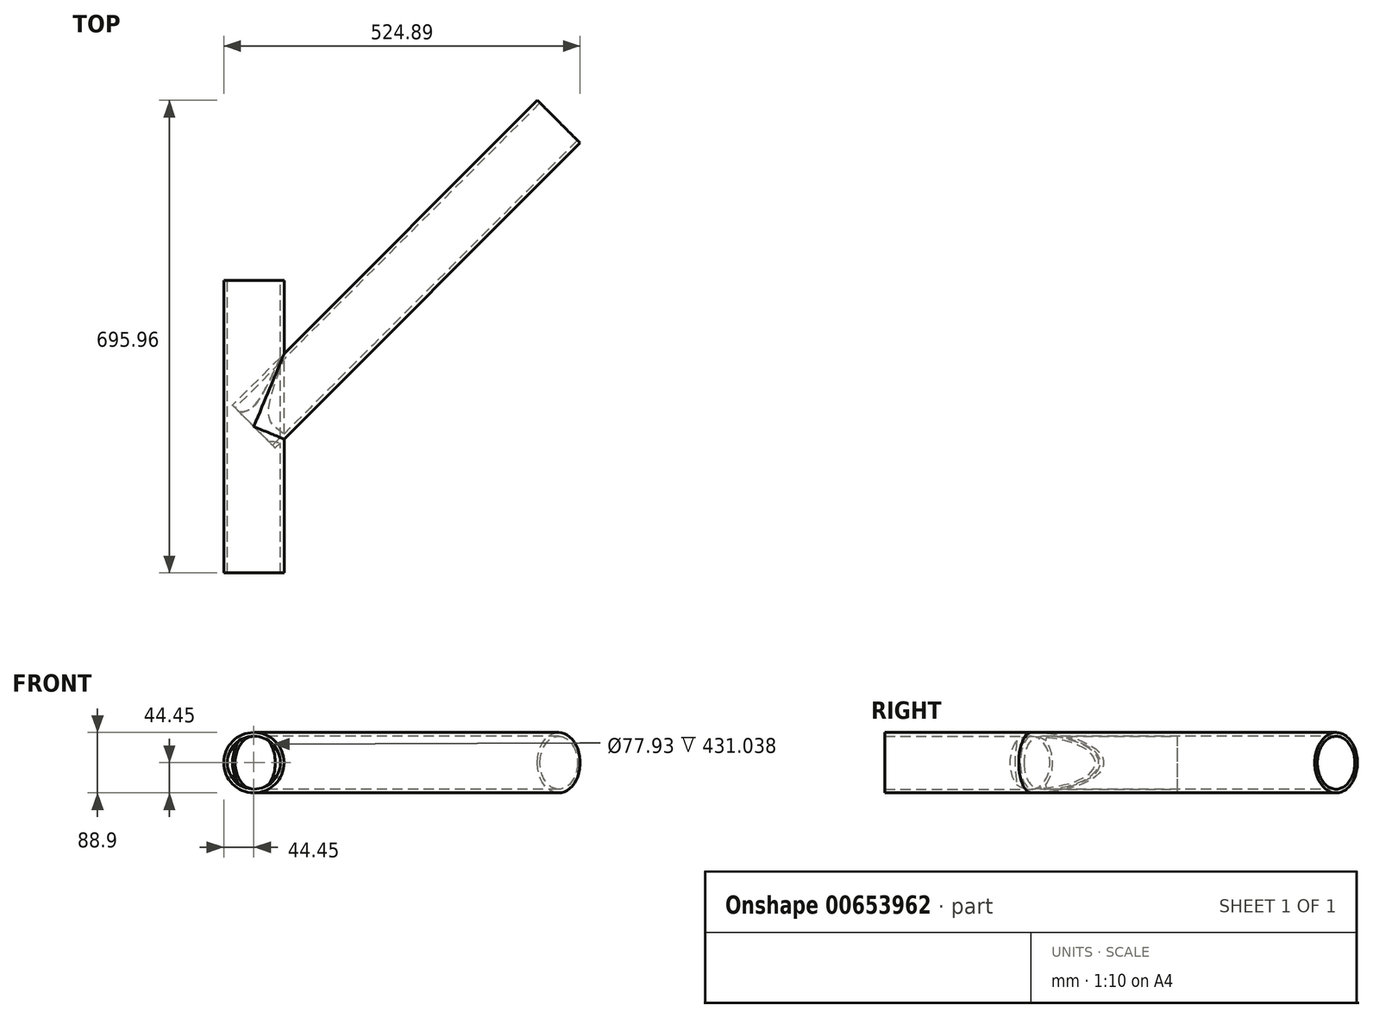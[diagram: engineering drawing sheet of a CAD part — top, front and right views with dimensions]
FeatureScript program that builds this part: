
annotation { "Feature Type Name" : "Feature", "Feature Type Description" : "" }
export const myFeature = defineFeature(function(context is Context, id is Id, definition is map)
    precondition{}
    {
        {
            var Q0;
            Q0=qCreatedBy(makeId("Front.planeOp"),FACE);
            var sketch = newSketch(context, id + "F0", { "sketchPlane" : qUnion([Q0])});
            skCircle(sketch, "E0", {"center": v(0, 0) * mm, "radius": 44.45 * mm});
            skCircle(sketch, "E1.0", {"center": v(0, 0) * mm, "radius": 38.96 * mm});
            skSolve(sketch);
        }
        {
            var Q0;
            Q0 = qSketchRegion(id + "F0", true);
            extrude(context, id + "F1", {"entities" : qUnion([Q0]), "depth" : 215.52 * mm, "offsetDistance" : 25.4 * mm, "hasSecondDirection" : true, "secondDirectionOppositeDirection" : true, "secondDirectionDepth" : 215.52 * mm});
        }
        {
            var Q0;
            Q0=qCreatedBy(makeId("Right.planeOp"),FACE);
            var Q1;
            Q1=qCreatedBy(makeId("Front.planeOp"),FACE);
            cPlane(context, id + "F2", {"entities" : qUnion([Q0, Q1]), "cplaneType" : CPlaneType.MID_PLANE, "offset" : 25.4 * mm, "width" : 152.4 * mm, "height" : 152.4 * mm});
        }
        {
            var Q0;
            Q0=qCreatedBy(id+"F2.planeOp",FACE);
            var sketch = newSketch(context, id + "F3", { "sketchPlane" : qUnion([Q0])});
            skCircle(sketch, "E2", {"center": v(0, 0) * mm, "radius": 44.45 * mm});
            skCircle(sketch, "E3.0", {"center": v(0, 0) * mm, "radius": 38.96 * mm});
            skSolve(sketch);
        }
        {
            var Q0;
            Q0 = qSketchRegion(id + "F3", true);
            extrude(context, id + "F4", {"entities" : qUnion([Q0]), "operationType" : NewBodyOperationType.ADD, "depth" : 635 * mm, "offsetDistance" : 25.4 * mm});
        }
    });
